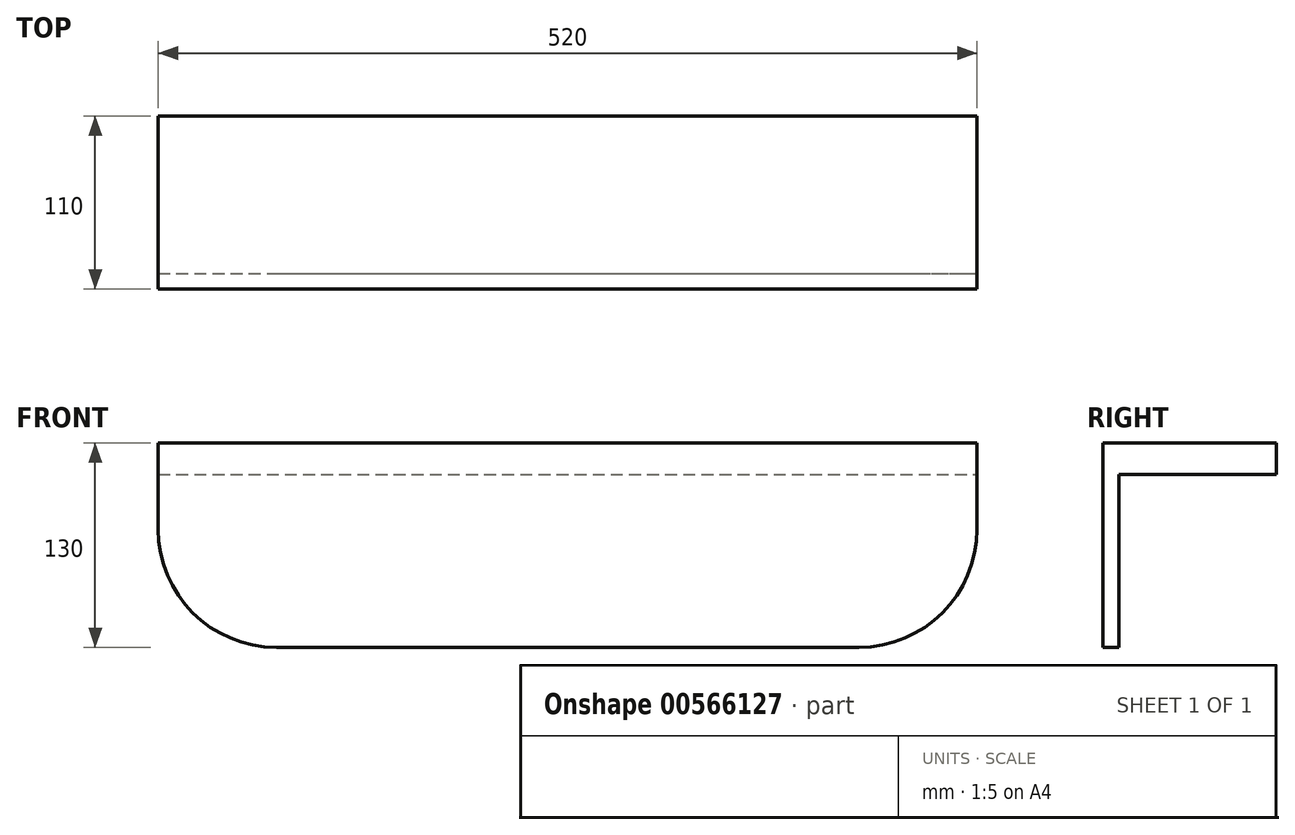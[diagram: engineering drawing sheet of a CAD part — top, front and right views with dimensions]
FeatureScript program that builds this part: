
annotation { "Feature Type Name" : "Feature", "Feature Type Description" : "" }
export const myFeature = defineFeature(function(context is Context, id is Id, definition is map)
    precondition{}
    {
        {
            var Q0;
            Q0=qCreatedBy(makeId("Front.planeOp"),FACE);
            var sketch = newSketch(context, id + "F0", { "sketchPlane" : qUnion([Q0])});
            skPoint(sketch, "E0.visualSharp", {"position": v(-250, -300) * mm});
            skPoint(sketch, "E1.visualSharp", {"position": v(250, -300) * mm});
            skLineSegment(sketch, "E2.0", {"start": v(-260, -180) * mm, "end": v(-260, -235) * mm});
            skLineSegment(sketch, "E2.1", {"start": v(260, -180) * mm, "end": v(260, -235) * mm});
            skArc(sketch, "E2.2", {"start": v(185, -310) * mm, "mid": v(238.03, -288.03) * mm, "end": v(260, -235) * mm});
            skLineSegment(sketch, "E2.3", {"start": v(-260, -180) * mm, "end": v(260, -180) * mm});
            skLineSegment(sketch, "E2.4", {"start": v(-185, -310) * mm, "end": v(185, -310) * mm});
            skArc(sketch, "E2.5", {"start": v(-260, -235) * mm, "mid": v(-238.03, -288.03) * mm, "end": v(-185, -310) * mm});
            skSolve(sketch);
        }
        {
            var Q0;
            Q0=makeQuery(id+"F0.imprint","IMPRINT",FACE,{"disambiguationData":[TD([[makeQuery(id+"F0.imprint","IMPRINT",EDGE,{"derivedFrom":sQuery(id+"F0.wireOp",EDGE,"E2.0")}),1.0]])]});
            extrude(context, id + "F1", {"entities" : qUnion([Q0]), "depth" : 10 * mm, "offsetDistance" : 25 * mm});
        }
        {
            var Q0;
            Q0=makeQuery(id+"F1.opExtrude","CAP_FACE",FACE,{"disambiguationData":[OSD([sQuery(id+"F0.wireOp",EDGE,"E2.0"),sQuery(id+"F0.wireOp",EDGE,"E2.1"),sQuery(id+"F0.wireOp",EDGE,"E2.2"),sQuery(id+"F0.wireOp",EDGE,"E2.3"),sQuery(id+"F0.wireOp",EDGE,"E2.4"),sQuery(id+"F0.wireOp",EDGE,"E2.5")])],"isStart":true});
            var sketch = newSketch(context, id + "F2", { "sketchPlane" : qUnion([Q0])});
            skLineSegment(sketch, "E3.0", {"start": v(260, -200) * mm, "end": v(-260, -200) * mm});
            skLineSegment(sketch, "E4", {"start": v(260, -200) * mm, "end": v(260, -180) * mm});
            skLineSegment(sketch, "E5", {"start": v(260, -180) * mm, "end": v(-260, -180) * mm});
            skLineSegment(sketch, "E6", {"start": v(-260, -180) * mm, "end": v(-260, -200) * mm});
            skSolve(sketch);
        }
        {
            var Q0;
            Q0=makeQuery(id+"F2.imprint","IMPRINT",FACE,{"disambiguationData":[TD([[makeQuery(id+"F2.imprint","IMPRINT",EDGE,{"derivedFrom":sQuery(id+"F2.wireOp",EDGE,"E3.0")}),-1.0]])]});
            extrude(context, id + "F3", {"entities" : qUnion([Q0]), "operationType" : NewBodyOperationType.ADD, "depth" : 100 * mm, "offsetDistance" : 25 * mm});
        }
    });
